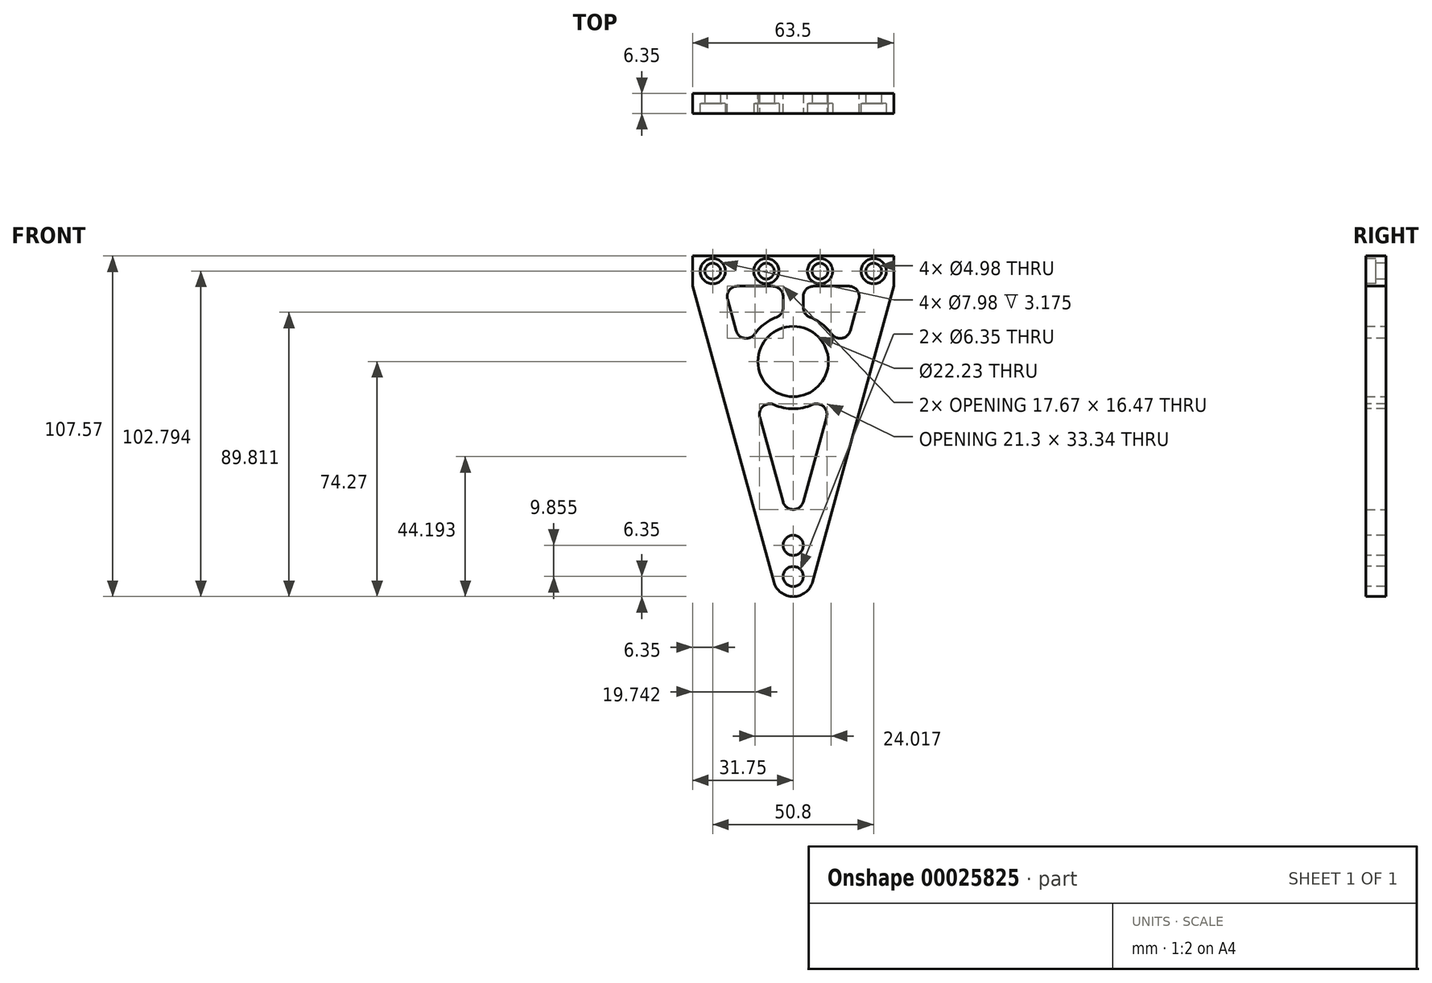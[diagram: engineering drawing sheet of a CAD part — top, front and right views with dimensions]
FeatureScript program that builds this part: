
annotation { "Feature Type Name" : "Feature", "Feature Type Description" : "" }
export const myFeature = defineFeature(function(context is Context, id is Id, definition is map)
    precondition{}
    {
        {
            var Q0;
            Q0=qCreatedBy(makeId("Front.planeOp"),FACE);
            var sketch = newSketch(context, id + "F0", { "sketchPlane" : qUnion([Q0])});
            skCircle(sketch, "E0", {"center": v(0, 0) * mm, "radius": 11.11 * mm});
            skLineSegment(sketch, "E1", {"start": v(0, 0) * mm, "end": v(59.72, 0) * mm, "construction": true});
            skLineSegment(sketch, "E2", {"start": v(0, 0) * mm, "end": v(0, 47.95) * mm, "construction": true});
            skLineSegment(sketch, "E3", {"start": v(-31.75, 33.3) * mm, "end": v(31.75, 33.3) * mm});
            skLineSegment(sketch, "E4", {"start": v(31.75, 33.3) * mm, "end": v(31.75, 23.77) * mm});
            skLineSegment(sketch, "E5", {"start": v(31.75, 23.77) * mm, "end": v(6.12, -69.6) * mm});
            skLineSegment(sketch, "E6", {"start": v(-6.12, -69.6) * mm, "end": v(-31.75, 23.77) * mm});
            skLineSegment(sketch, "E7", {"start": v(-31.75, 23.77) * mm, "end": v(-31.75, 33.3) * mm});
            skArc(sketch, "E8", {"start": v(-6.12, -69.6) * mm, "mid": v(0, -74.27) * mm, "end": v(6.12, -69.6) * mm});
            skSolve(sketch);
        }
        {
            var Q0;
            Q0=makeQuery(id+"F0.imprint","IMPRINT",FACE,{"disambiguationData":[TD([[makeQuery(id+"F0.imprint","IMPRINT",EDGE,{"derivedFrom":sQuery(id+"F0.wireOp",EDGE,"E0")}),-1.0]])]});
            extrude(context, id + "F1", {"entities" : qUnion([Q0]), "depth" : 6.35 * mm});
        }
        {
            var Q0;
            Q0=makeQuery(id+"F1.opExtrude","CAP_FACE",FACE,{"disambiguationData":[OSD([sQuery(id+"F0.wireOp",EDGE,"E0"),sQuery(id+"F0.wireOp",EDGE,"E3"),sQuery(id+"F0.wireOp",EDGE,"E4"),sQuery(id+"F0.wireOp",EDGE,"E5"),sQuery(id+"F0.wireOp",EDGE,"E6"),sQuery(id+"F0.wireOp",EDGE,"E7"),sQuery(id+"F0.wireOp",EDGE,"E8")])],"isStart":false});
            var sketch = newSketch(context, id + "F2", { "sketchPlane" : qUnion([Q0])});
            skLineSegment(sketch, "E9.0", {"start": v(21.87, 23.77) * mm, "end": v(3.18, 23.77) * mm});
            skLineSegment(sketch, "E9.2", {"start": v(0, -55.92) * mm, "end": v(13.77, -5.75) * mm});
            skLineSegment(sketch, "E9.3", {"start": v(-21.87, 23.77) * mm, "end": v(-14.78, -2.08) * mm});
            skArc(sketch, "E10", {"start": v(14.78, -2.08) * mm, "mid": v(12.25, 8.53) * mm, "end": v(3.18, 14.58) * mm});
            skLineSegment(sketch, "E11.trimOffspring", {"start": v(14.78, -2.08) * mm, "end": v(21.87, 23.77) * mm});
            skLineSegment(sketch, "E12.trimOffspring", {"start": v(-13.77, -5.75) * mm, "end": v(0, -55.92) * mm});
            skArc(sketch, "E13.trimOffspring", {"start": v(-13.77, -5.75) * mm, "mid": v(0, -14.92) * mm, "end": v(13.77, -5.75) * mm});
            skLineSegment(sketch, "E14", {"start": v(0, 0) * mm, "end": v(0, 45.4) * mm, "construction": true});
            skLineSegment(sketch, "E15", {"start": v(-3.17, 23.77) * mm, "end": v(-3.18, 14.58) * mm});
            skLineSegment(sketch, "E16", {"start": v(3.17, 23.77) * mm, "end": v(3.18, 14.58) * mm});
            skLineSegment(sketch, "E17.trimOffspring", {"start": v(-3.18, 23.77) * mm, "end": v(-21.87, 23.77) * mm});
            skArc(sketch, "E18.trimOffspring", {"start": v(-3.18, 14.58) * mm, "mid": v(-12.25, 8.53) * mm, "end": v(-14.78, -2.08) * mm});
            skSolve(sketch);
        }
        {
            var Q0;
            Q0=makeQuery(id+"F2.imprint","IMPRINT",FACE,{"disambiguationData":[TD([[makeQuery(id+"F2.imprint","IMPRINT",EDGE,{"derivedFrom":sQuery(id+"F2.wireOp",EDGE,"E9.3")}),1.0]])]});
            var Q1;
            Q1=makeQuery(id+"F2.imprint","IMPRINT",FACE,{"disambiguationData":[TD([[makeQuery(id+"F2.imprint","IMPRINT",EDGE,{"derivedFrom":sQuery(id+"F2.wireOp",EDGE,"E9.0")}),1.0]])]});
            var Q2;
            Q2=makeQuery(id+"F2.imprint","IMPRINT",FACE,{"disambiguationData":[TD([[makeQuery(id+"F2.imprint","IMPRINT",EDGE,{"derivedFrom":sQuery(id+"F2.wireOp",EDGE,"E9.2")}),1.0]])]});
            extrude(context, id + "F3", {"entities" : qUnion([Q0, Q1, Q2]), "operationType" : NewBodyOperationType.REMOVE, "endBound" : BoundingType.THROUGH_ALL, "oppositeDirection" : true, "depth" : 25.4 * mm});
        }
        {
            var Q0;
            Q0=makeQuery(id+"F3.boolean.opBoolean","COPY",EDGE,{"derivedFrom":makeQuery(id+"F3.opExtrude","SWEPT_EDGE",EDGE,{"disambiguationData":[OSD([sQuery(id+"F2.wireOp",EDGE,"E9.3"),sQuery(id+"F2.wireOp",EDGE,"E17.trimOffspring")])]})});
            var Q1;
            Q1=makeQuery(id+"F3.boolean.opBoolean","COPY",EDGE,{"derivedFrom":makeQuery(id+"F3.opExtrude","SWEPT_EDGE",EDGE,{"disambiguationData":[OSD([sQuery(id+"F2.wireOp",EDGE,"E9.3"),sQuery(id+"F2.wireOp",EDGE,"E18.trimOffspring")])]})});
            var Q2;
            Q2=makeQuery(id+"F3.boolean.opBoolean","COPY",EDGE,{"derivedFrom":makeQuery(id+"F3.opExtrude","SWEPT_EDGE",EDGE,{"disambiguationData":[OSD([sQuery(id+"F2.wireOp",EDGE,"E15"),sQuery(id+"F2.wireOp",EDGE,"E17.trimOffspring")])]})});
            var Q3;
            Q3=makeQuery(id+"F3.boolean.opBoolean","COPY",EDGE,{"derivedFrom":makeQuery(id+"F3.opExtrude","SWEPT_EDGE",EDGE,{"disambiguationData":[OSD([sQuery(id+"F2.wireOp",EDGE,"E15"),sQuery(id+"F2.wireOp",EDGE,"E18.trimOffspring")])]})});
            var Q4;
            Q4=makeQuery(id+"F3.boolean.opBoolean","COPY",EDGE,{"derivedFrom":makeQuery(id+"F3.opExtrude","SWEPT_EDGE",EDGE,{"disambiguationData":[OSD([sQuery(id+"F2.wireOp",EDGE,"E10"),sQuery(id+"F2.wireOp",EDGE,"E16")])]})});
            var Q5;
            Q5=makeQuery(id+"F3.boolean.opBoolean","COPY",EDGE,{"derivedFrom":makeQuery(id+"F3.opExtrude","SWEPT_EDGE",EDGE,{"disambiguationData":[OSD([sQuery(id+"F2.wireOp",EDGE,"E10"),sQuery(id+"F2.wireOp",EDGE,"E11.trimOffspring")])]})});
            var Q6;
            Q6=makeQuery(id+"F3.boolean.opBoolean","COPY",EDGE,{"derivedFrom":makeQuery(id+"F3.opExtrude","SWEPT_EDGE",EDGE,{"disambiguationData":[OSD([sQuery(id+"F2.wireOp",EDGE,"E9.0"),sQuery(id+"F2.wireOp",EDGE,"E16")])]})});
            var Q7;
            Q7=makeQuery(id+"F3.boolean.opBoolean","COPY",EDGE,{"derivedFrom":makeQuery(id+"F3.opExtrude","SWEPT_EDGE",EDGE,{"disambiguationData":[OSD([sQuery(id+"F2.wireOp",EDGE,"E9.0"),sQuery(id+"F2.wireOp",EDGE,"E11.trimOffspring")])]})});
            var Q8;
            Q8=makeQuery(id+"F3.boolean.opBoolean","COPY",EDGE,{"derivedFrom":makeQuery(id+"F3.opExtrude","SWEPT_EDGE",EDGE,{"disambiguationData":[OSD([sQuery(id+"F2.wireOp",EDGE,"E9.2"),sQuery(id+"F2.wireOp",EDGE,"E12.trimOffspring")])]})});
            var Q9;
            Q9=makeQuery(id+"F3.boolean.opBoolean","COPY",EDGE,{"derivedFrom":makeQuery(id+"F3.opExtrude","SWEPT_EDGE",EDGE,{"disambiguationData":[OSD([sQuery(id+"F2.wireOp",EDGE,"E12.trimOffspring"),sQuery(id+"F2.wireOp",EDGE,"E13.trimOffspring")])]})});
            var Q10;
            Q10=makeQuery(id+"F3.boolean.opBoolean","COPY",EDGE,{"derivedFrom":makeQuery(id+"F3.opExtrude","SWEPT_EDGE",EDGE,{"disambiguationData":[OSD([sQuery(id+"F2.wireOp",EDGE,"E9.2"),sQuery(id+"F2.wireOp",EDGE,"E13.trimOffspring")])]})});
            fillet(context, id + "F4", {"entities" : qUnion([Q0, Q1, Q2, Q3, Q4, Q5, Q6, Q7, Q8, Q9, Q10]), "radius" : 3.3 * mm, "tangentPropagation" : true, "allowEdgeOverflow" : false});
        }
        {
            var Q0;
            Q0=makeQuery(id+"F1.opExtrude","CAP_FACE",FACE,{"disambiguationData":[OSD([sQuery(id+"F0.wireOp",EDGE,"E0"),sQuery(id+"F0.wireOp",EDGE,"E3"),sQuery(id+"F0.wireOp",EDGE,"E4"),sQuery(id+"F0.wireOp",EDGE,"E5"),sQuery(id+"F0.wireOp",EDGE,"E6"),sQuery(id+"F0.wireOp",EDGE,"E7"),sQuery(id+"F0.wireOp",EDGE,"E8")])],"isStart":false});
            var sketch = newSketch(context, id + "F5", { "sketchPlane" : qUnion([Q0])});
            skLineSegment(sketch, "E19", {"start": v(-25.4, 28.52) * mm, "end": v(-8.47, 28.52) * mm});
            skLineSegment(sketch, "E20", {"start": v(-8.47, 28.52) * mm, "end": v(8.47, 28.52) * mm});
            skLineSegment(sketch, "E21", {"start": v(8.47, 28.52) * mm, "end": v(25.4, 28.52) * mm});
            skLineSegment(sketch, "E22", {"start": v(0, 28.52) * mm, "end": v(0, -67.92) * mm});
            skPoint(sketch, "E23", {"position": v(0, -58.06) * mm});
            skSolve(sketch);
        }
        {
            var Q0;
            Q0=sQuery(id+"F5.wireOp",VERTEX,"E19.start");
            var Q1;
            Q1=sQuery(id+"F5.wireOp",VERTEX,"E20.start");
            var Q2;
            Q2=sQuery(id+"F5.wireOp",VERTEX,"E21.start");
            var Q3;
            Q3=sQuery(id+"F5.wireOp",VERTEX,"E21.end");
            var Q4;
            Q4=makeQuery(id+"F1.opExtrude","SWEPT_BODY",BODY,{"disambiguationData":[OSD([sQuery(id+"F0.wireOp",EDGE,"E0"),sQuery(id+"F0.wireOp",EDGE,"E3"),sQuery(id+"F0.wireOp",EDGE,"E4"),sQuery(id+"F0.wireOp",EDGE,"E5"),sQuery(id+"F0.wireOp",EDGE,"E6"),sQuery(id+"F0.wireOp",EDGE,"E7"),sQuery(id+"F0.wireOp",EDGE,"E8")])]});
            hole(context, id + "F6", {"style" : HoleStyle.C_BORE, "holeDiameter" : 4.98 * mm, "cBoreDiameter" : 7.98 * mm, "cBoreDepth" : 3.17 * mm, "endStyle" : HoleEndStyle.THROUGH, "locations" : qUnion([Q0, Q1, Q2, Q3]), "scope" : qUnion([Q4])});
        }
        {
            var Q0;
            Q0=sQuery(id+"F5.wireOp",VERTEX,"E23");
            var Q1;
            Q1=sQuery(id+"F5.wireOp",VERTEX,"E22.end");
            var Q2;
            Q2=makeQuery(id+"F1.opExtrude","SWEPT_BODY",BODY,{"disambiguationData":[OSD([sQuery(id+"F0.wireOp",EDGE,"E0"),sQuery(id+"F0.wireOp",EDGE,"E3"),sQuery(id+"F0.wireOp",EDGE,"E4"),sQuery(id+"F0.wireOp",EDGE,"E5"),sQuery(id+"F0.wireOp",EDGE,"E6"),sQuery(id+"F0.wireOp",EDGE,"E7"),sQuery(id+"F0.wireOp",EDGE,"E8")])]});
            hole(context, id + "F7", {"style" : HoleStyle.SIMPLE, "holeDiameter" : 6.35 * mm, "endStyle" : HoleEndStyle.THROUGH, "locations" : qUnion([Q0, Q1]), "scope" : qUnion([Q2])});
        }
    });
